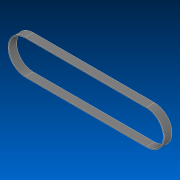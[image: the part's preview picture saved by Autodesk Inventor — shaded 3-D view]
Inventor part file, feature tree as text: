
AUTODESK INVENTOR PART (.ipt)
format: ipt  version: 2022.2 (Build 262287000, 287)  size: 95,232 bytes
history: native  units: in
note: dims shown in document units (in); Inventor stores cm internally (conversion verified against a paired STEP export)
features: extrude x1, sketch x1
ambient origin geometry x8: Origin, YZ Plane, XZ Plane, XY Plane, X Axis, Y Axis, Z Axis, Center Point
bodies: Solid1 (feature_tree)
feature tree (2):
  extrude  "Extrusion1"  Depth=1.504in
  sketch  "Sketch1"  dims[d0=5.5in d1=1.504in d2=0.0394in d3=0.3543in d4=0.0in]
